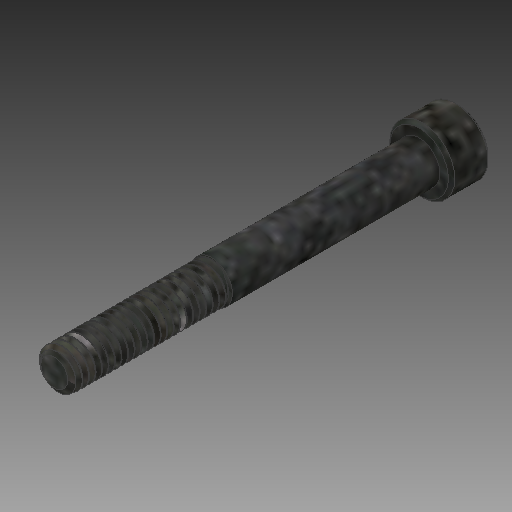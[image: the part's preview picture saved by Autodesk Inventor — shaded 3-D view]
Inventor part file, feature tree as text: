
AUTODESK INVENTOR PART (.ipt)
format: ipt  version: 2018 (Build 220112000, 112)  size: 732,160 bytes
history: native  units: in
note: dims shown in document units (in); Inventor stores cm internally (conversion verified against a paired STEP export)
features: chamfer x1
ambient origin geometry x8: Origin, YZ Plane, XZ Plane, XY Plane, X Axis, Y Axis, Z Axis, Center Point
bodies: Solid1 (feature_tree)
feature tree (1):
  chamfer  "Chamfer1"  [1 undecoded]
note: 1 required parameter value undecoded (feature->parameter linkage not recoverable at this tier; creation-order binding heuristic only, values carry confidence <= 0.55)
